# Revit family: TZF NAO P
name_source: partatom
category: Aparatos sanitarios
units: mm (PartAtom-declared; Revit-internal decimal feet)

## family parameters
Activar corte en vistas = No
Compartido = No
Corte con vacíos al cargar = No
Cota de conector redondo = Usar diámetro
Mantener orientación de anotación = No
Número OmniClass = 23.45.00.00
Punto de cálculo de habitación = No
Se basa en plano de trabajo = No
Siempre vertical = Sí
Tipo de pieza = Normal
Título OmniClass = Sanitary, Laundry, and Cleaning Equipment

## types (1)
- TZF NAO P
    Accessories = Se recomienda instalar con el soporte
S-TZF-P (no incluído), para lograr las alturas de 15,5" o 17".
    Ceramic Warranty = Helvex, S. A. de C. V. garantiza sus productos
cerámicos como libres de defectos en materiales,
mano de obra y procesos de fabricación por un
periodo de 65 años.
En los herrajes por defectos de manufactura por 5
años.
El dispositivo TDS en el mingitorio seco por 3
años.
Tapa y asiento por un periodo de 2 años.
La vigencia de la garantía inicia a partir de la fecha
de entrega del producto al consumidor indicada en
esta Póliza de Garantía.
    Comentarios de tipo = Ceramic
    Compliance = NOM-009-CONAGUA-2001
    Descripción = Taza para Fluxómetro a Pared,
3,5, 4,8, y 6 LPD, Color Blanco
3,5, 4,8, y 6 LPD, Color Blanco
    Elevación por defecto = 16"
    Fabricante = HELVEX
    Features = Diseño ergonómico, Máxima eficiencia en descarga, Mueble libre de alabeo (base plana), Cerámica porcelanizada de alto brillo, Calidad (A), Descarga tipo Turvex con jet, Espejo de agua óptimo.
    High Gloss Ceramic = High Gloss
    Installation Adjustment = Toilet Holder: Wall-Mount; Pipe Coupling: Spud Of Ø 1 ½" (38 mm) And Ø 1 ¼" (32 mm)
    Maximum Consumption = 1,26 gpf
    Modelo = TZF NAO P
    Presión de Trabajo = Pmin.= 2,0 kg/cm² para 3,5 LPD
Pmin.= 1,4 kg/cm² para 4,8 y 6 LPD
Pmax.= 6,0 kg/cm²
    Total Height = 15"
    Total Length = 26"
    Total Width = 16"
    URL = https://helvex.com.mx

## geometry (parser evidence)
native form markers: Sweep x3
no freeform markers — native parametric forms only
